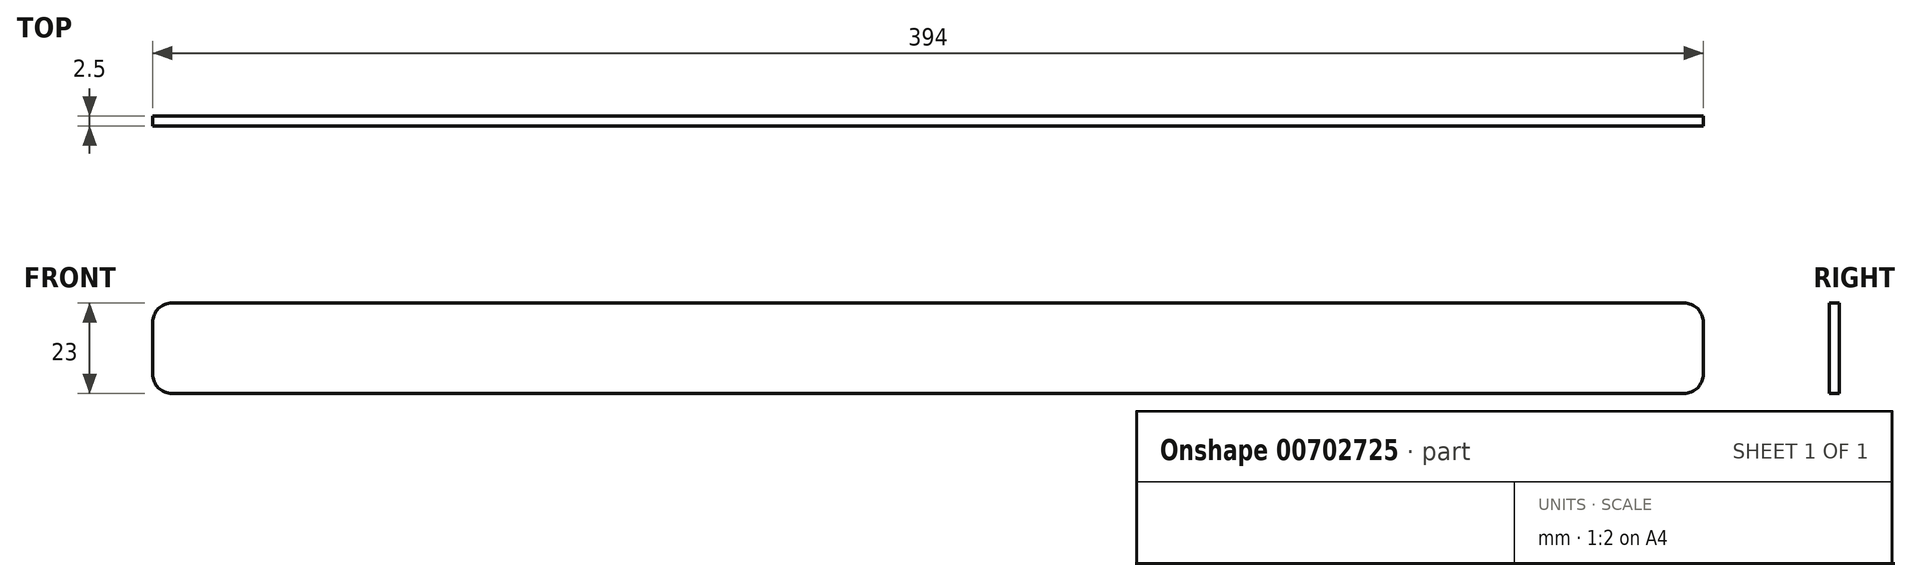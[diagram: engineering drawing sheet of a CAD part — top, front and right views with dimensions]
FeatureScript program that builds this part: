
annotation { "Feature Type Name" : "Feature", "Feature Type Description" : "" }
export const myFeature = defineFeature(function(context is Context, id is Id, definition is map)
    precondition{}
    {
        {
            var Q0;
            Q0=qCreatedBy(makeId("Front.planeOp"),FACE);
            var sketch = newSketch(context, id + "F0", { "sketchPlane" : qUnion([Q0])});
            skLineSegment(sketch, "E0.bottom", {"start": v(-197, 11.5) * mm, "end": v(197, 11.5) * mm});
            skLineSegment(sketch, "E0.top", {"start": v(-197, -11.5) * mm, "end": v(197, -11.5) * mm});
            skLineSegment(sketch, "E0.left", {"start": v(-197, 11.5) * mm, "end": v(-197, -11.5) * mm});
            skLineSegment(sketch, "E0.right", {"start": v(197, 11.5) * mm, "end": v(197, -11.5) * mm});
            skPoint(sketch, "E0.middle", {"position": v(0, 0) * mm});
            skSolve(sketch);
        }
        {
            var Q0;
            Q0=makeQuery(id+"F0.imprint","IMPRINT",FACE,{"disambiguationData":[TD([[makeQuery(id+"F0.imprint","IMPRINT",EDGE,{"derivedFrom":sQuery(id+"F0.wireOp",EDGE,"E0.bottom")}),-1.0]])]});
            extrude(context, id + "F1", {"entities" : qUnion([Q0]), "endBound" : BoundingType.SYMMETRIC, "depth" : 2.5 * mm, "offsetDistance" : 25 * mm});
        }
        {
            var Q0;
            Q0=makeQuery(id+"F1.opExtrude","SWEPT_EDGE",EDGE,{"disambiguationData":[OSD([sQuery(id+"F0.wireOp",EDGE,"E0.bottom"),sQuery(id+"F0.wireOp",EDGE,"E0.left")])]});
            var Q1;
            Q1=makeQuery(id+"F1.opExtrude","SWEPT_EDGE",EDGE,{"disambiguationData":[OSD([sQuery(id+"F0.wireOp",EDGE,"E0.top"),sQuery(id+"F0.wireOp",EDGE,"E0.left")])]});
            var Q2;
            Q2=makeQuery(id+"F1.opExtrude","SWEPT_EDGE",EDGE,{"disambiguationData":[OSD([sQuery(id+"F0.wireOp",EDGE,"E0.bottom"),sQuery(id+"F0.wireOp",EDGE,"E0.right")])]});
            var Q3;
            Q3=makeQuery(id+"F1.opExtrude","SWEPT_EDGE",EDGE,{"disambiguationData":[OSD([sQuery(id+"F0.wireOp",EDGE,"E0.top"),sQuery(id+"F0.wireOp",EDGE,"E0.right")])]});
            fillet(context, id + "F2", {"entities" : qUnion([Q0, Q1, Q2, Q3]), "radius" : 5 * mm, "tangentPropagation" : true, "allowEdgeOverflow" : false});
        }
    });
